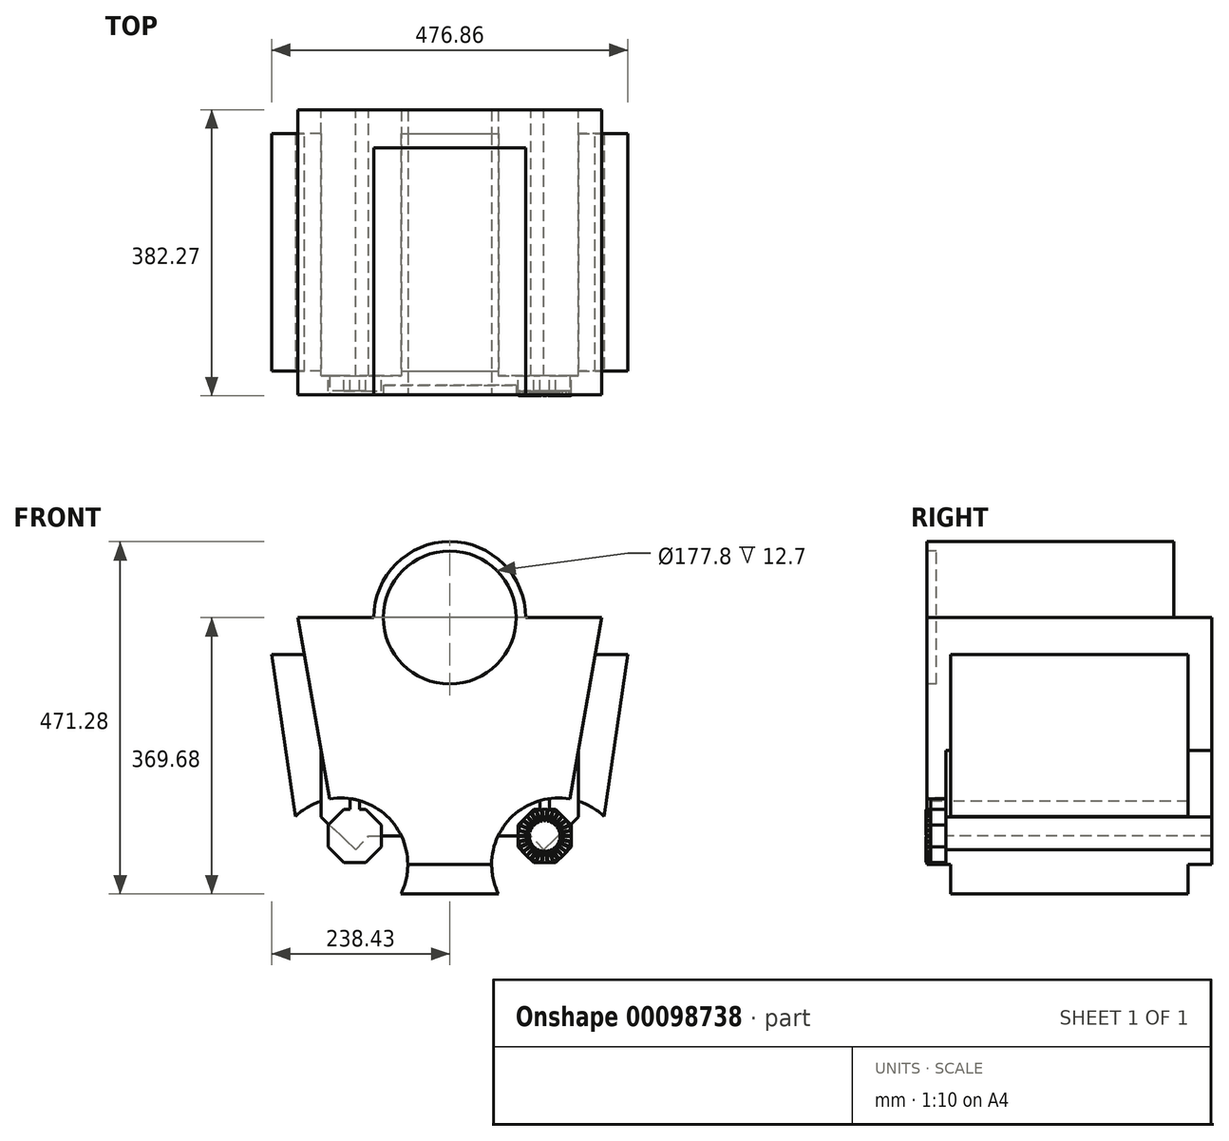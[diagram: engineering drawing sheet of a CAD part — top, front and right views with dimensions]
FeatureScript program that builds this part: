
annotation { "Feature Type Name" : "Feature", "Feature Type Description" : "" }
export const myFeature = defineFeature(function(context is Context, id is Id, definition is map)
    precondition{}
    {
        {
            var Q0;
            Q0=qCreatedBy(makeId("Front.planeOp"),FACE);
            var sketch = newSketch(context, id + "F0", { "sketchPlane" : qUnion([Q0])});
            skLineSegment(sketch, "E0", {"start": v(-144.98, -152.4) * mm, "end": v(-203.2, 177.8) * mm});
            skLineSegment(sketch, "E1", {"start": v(-203.2, 177.8) * mm, "end": v(0, 177.8) * mm});
            skLineSegment(sketch, "E2", {"start": v(-144.98, -152.4) * mm, "end": v(0, -152.4) * mm});
            skLineSegment(sketch, "E3", {"start": v(0, 177.8) * mm, "end": v(0, -152.4) * mm, "construction": true});
            skLineSegment(sketch, "E4.MirrorCS", {"start": v(203.2, 177.8) * mm, "end": v(0, 177.8) * mm});
            skLineSegment(sketch, "E5.MirrorCS", {"start": v(144.98, -152.4) * mm, "end": v(0, -152.4) * mm});
            skLineSegment(sketch, "E6.MirrorCS", {"start": v(144.98, -152.4) * mm, "end": v(203.2, 177.8) * mm});
            skSolve(sketch);
        }
        {
            var Q0;
            Q0=makeQuery(id+"F0.imprint","IMPRINT",FACE,{"disambiguationData":[TD([[makeQuery(id+"F0.imprint","IMPRINT",EDGE,{"derivedFrom":sQuery(id+"F0.wireOp",EDGE,"E0")}),-1.0]])]});
            extrude(context, id + "F1", {"entities" : qUnion([Q0]), "endBound" : BoundingType.SYMMETRIC, "depth" : 381 * mm});
        }
        {
            var Q0;
            Q0=qCreatedBy(makeId("Front.planeOp"),FACE);
            var sketch = newSketch(context, id + "F2", { "sketchPlane" : qUnion([Q0])});
            skLineSegment(sketch, "E7", {"start": v(-238.43, 128.66) * mm, "end": v(-190.8, -191.88) * mm});
            skLineSegment(sketch, "E8.MirrorCS", {"start": v(238.43, 128.66) * mm, "end": v(190.8, -191.88) * mm});
            skLineSegment(sketch, "E9", {"start": v(-238.43, 128.66) * mm, "end": v(238.43, 128.66) * mm});
            skLineSegment(sketch, "E10", {"start": v(-190.8, -191.88) * mm, "end": v(190.8, -191.88) * mm});
            skSolve(sketch);
        }
        {
            var Q0;
            Q0 = qSketchRegion(id + "F2", true);
            extrude(context, id + "F3", {"entities" : qUnion([Q0]), "operationType" : NewBodyOperationType.ADD, "endBound" : BoundingType.SYMMETRIC, "depth" : 317.5 * mm});
        }
        {
            var Q0;
            Q0=makeQuery(id+"F1.opExtrude","CAP_FACE",FACE,{"disambiguationData":[OSD([sQuery(id+"F0.wireOp",EDGE,"E0"),sQuery(id+"F0.wireOp",EDGE,"E1"),sQuery(id+"F0.wireOp",EDGE,"E2"),sQuery(id+"F0.wireOp",EDGE,"E4.MirrorCS"),sQuery(id+"F0.wireOp",EDGE,"E5.MirrorCS"),sQuery(id+"F0.wireOp",EDGE,"E6.MirrorCS")])],"isStart":false});
            var sketch = newSketch(context, id + "F4", { "sketchPlane" : qUnion([Q0])});
            skCircle(sketch, "E11", {"center": v(0, 177.8) * mm, "radius": 101.6 * mm});
            skSolve(sketch);
        }
        {
            var Q0;
            Q0 = qSketchRegion(id + "F4", true);
            extrude(context, id + "F5", {"entities" : qUnion([Q0]), "operationType" : NewBodyOperationType.ADD, "oppositeDirection" : true, "depth" : 330.2 * mm});
        }
        {
            var Q0;
            Q0=makeQuery(id+"F5.boolean.opBoolean","MERGE",FACE,{"derivedFrom":[makeQuery(id+"F1.opExtrude","CAP_FACE",FACE,{"disambiguationData":[OSD([sQuery(id+"F0.wireOp",EDGE,"E0"),sQuery(id+"F0.wireOp",EDGE,"E1"),sQuery(id+"F0.wireOp",EDGE,"E2"),sQuery(id+"F0.wireOp",EDGE,"E4.MirrorCS"),sQuery(id+"F0.wireOp",EDGE,"E5.MirrorCS"),sQuery(id+"F0.wireOp",EDGE,"E6.MirrorCS")])],"isStart":false}),makeQuery(id+"F5.opExtrude","CAP_FACE",FACE,{"disambiguationData":[OSD([sQuery(id+"F4.wireOp",EDGE,"E11")])],"isStart":true})]});
            var sketch = newSketch(context, id + "F6", { "sketchPlane" : qUnion([Q0])});
            skCircle(sketch, "E12", {"center": v(144.98, -152.4) * mm, "radius": 88.9 * mm});
            skCircle(sketch, "E13", {"center": v(-144.98, -152.4) * mm, "radius": 88.9 * mm});
            skSolve(sketch);
        }
        {
            var Q0;
            Q0 = qSketchRegion(id + "F6", true);
            extrude(context, id + "F7", {"entities" : qUnion([Q0]), "operationType" : NewBodyOperationType.REMOVE, "endBound" : BoundingType.THROUGH_ALL, "oppositeDirection" : true, "depth" : 381 * mm});
        }
        {
            var Q0;
            Q0=makeQuery(id+"F5.boolean.opBoolean","MERGE",FACE,{"derivedFrom":[makeQuery(id+"F1.opExtrude","CAP_FACE",FACE,{"disambiguationData":[OSD([sQuery(id+"F0.wireOp",EDGE,"E0"),sQuery(id+"F0.wireOp",EDGE,"E1"),sQuery(id+"F0.wireOp",EDGE,"E2"),sQuery(id+"F0.wireOp",EDGE,"E4.MirrorCS"),sQuery(id+"F0.wireOp",EDGE,"E5.MirrorCS"),sQuery(id+"F0.wireOp",EDGE,"E6.MirrorCS")])],"isStart":false}),makeQuery(id+"F5.opExtrude","CAP_FACE",FACE,{"disambiguationData":[OSD([sQuery(id+"F4.wireOp",EDGE,"E11")])],"isStart":true})]});
            var sketch = newSketch(context, id + "F8", { "sketchPlane" : qUnion([Q0])});
            skCircle(sketch, "E14", {"center": v(0, 177.8) * mm, "radius": 88.9 * mm});
            skSolve(sketch);
        }
        {
            var Q0;
            Q0 = qSketchRegion(id + "F8", true);
            extrude(context, id + "F9", {"entities" : qUnion([Q0]), "operationType" : NewBodyOperationType.REMOVE, "oppositeDirection" : true, "depth" : 12.7 * mm});
        }
        {
            var Q0;
            Q0=qCreatedBy(makeId("Front.planeOp"),FACE);
            var sketch = newSketch(context, id + "F10", { "sketchPlane" : qUnion([Q0])});
            skLineSegment(sketch, "E15.bottom", {"start": v(-171.85, 0) * mm, "end": v(171.85, 0) * mm});
            skLineSegment(sketch, "E15.left", {"start": v(-171.85, 0) * mm, "end": v(-171.85, -88.9) * mm});
            skLineSegment(sketch, "E15.right", {"start": v(171.85, 0) * mm, "end": v(171.85, -88.9) * mm});
            skLineSegment(sketch, "E16", {"start": v(-171.85, -88.9) * mm, "end": v(-125.87, -132.7) * mm});
            skLineSegment(sketch, "E17", {"start": v(-125.87, -132.7) * mm, "end": v(-108.35, -114.3) * mm});
            skLineSegment(sketch, "E18", {"start": v(0, -153.35) * mm, "end": v(0, 168.6) * mm, "construction": true});
            skPoint(sketch, "E18.endSnap0", {"position": v(0, -153.35) * mm});
            skLineSegment(sketch, "E19.MirrorCS", {"start": v(125.87, -132.7) * mm, "end": v(108.35, -114.3) * mm});
            skLineSegment(sketch, "E20.MirrorCS", {"start": v(171.85, -88.9) * mm, "end": v(125.87, -132.7) * mm});
            skLineSegment(sketch, "E21", {"start": v(-108.35, -114.3) * mm, "end": v(108.35, -114.3) * mm});
            skSolve(sketch);
        }
        {
            var Q0;
            Q0 = qSketchRegion(id + "F10", true);
            extrude(context, id + "F11", {"entities" : qUnion([Q0]), "operationType" : NewBodyOperationType.ADD, "depth" : 165.1 * mm, "hasSecondDirection" : true, "secondDirectionOppositeDirection" : true, "secondDirectionDepth" : 190.5 * mm});
        }
        {
            var Q0;
            {var subQ0=sQuery(id+"F10.wireOp",EDGE,"E19.MirrorCS");var subQ1=sQuery(id+"F10.wireOp",EDGE,"E21");var subQ2=sQuery(id+"F10.wireOp",EDGE,"E15.right");var subQ3=sQuery(id+"F10.wireOp",EDGE,"E20.MirrorCS");Q0=makeQuery(id+"F11.boolean.opBoolean","SPLIT",FACE,{"disambiguationData":[TD([makeQuery(id+"F1.opExtrude","SWEPT_FACE",FACE,{"disambiguationData":[OSD([sQuery(id+"F0.wireOp",EDGE,"E6.MirrorCS")])]})])],"derivedFrom":makeQuery(id+"F11.opExtrude","CAP_FACE",FACE,{"disambiguationData":[OSD([sQuery(id+"F10.wireOp",EDGE,"E15.bottom"),sQuery(id+"F10.wireOp",EDGE,"E15.left"),subQ2,sQuery(id+"F10.wireOp",EDGE,"E16"),sQuery(id+"F10.wireOp",EDGE,"E17"),subQ0,subQ3,subQ1])],"isStart":false})});}
            var sketch = newSketch(context, id + "F12", { "sketchPlane" : qUnion([Q0])});
            skCircle(sketch, "E22.cCircle", {"center": v(127, -114.3) * mm, "radius": 35.56 * mm, "construction": true});
            skLineSegment(sketch, "E22.0", {"start": v(112.27, -78.74) * mm, "end": v(120.65, -78.74) * mm});
            skLineSegment(sketch, "E22.1", {"start": v(141.73, -78.74) * mm, "end": v(162.56, -99.57) * mm});
            skLineSegment(sketch, "E22.2", {"start": v(162.56, -99.57) * mm, "end": v(162.56, -129.03) * mm});
            skLineSegment(sketch, "E22.3", {"start": v(162.56, -129.03) * mm, "end": v(141.73, -149.86) * mm});
            skLineSegment(sketch, "E22.4", {"start": v(141.73, -149.86) * mm, "end": v(112.27, -149.86) * mm});
            skLineSegment(sketch, "E22.5", {"start": v(112.27, -149.86) * mm, "end": v(91.44, -129.03) * mm});
            skLineSegment(sketch, "E22.6", {"start": v(91.44, -129.03) * mm, "end": v(91.44, -99.57) * mm});
            skLineSegment(sketch, "E22.7", {"start": v(91.44, -99.57) * mm, "end": v(112.27, -78.74) * mm});
            skPoint(sketch, "E22.0.midPoint", {"position": v(127, -78.74) * mm});
            skLineSegment(sketch, "E23", {"start": v(120.65, -78.74) * mm, "end": v(120.65, -66.9) * mm});
            skLineSegment(sketch, "E24", {"start": v(133.35, -78.74) * mm, "end": v(133.35, -64.26) * mm});
            skArc(sketch, "E25", {"start": v(133.35, -64.26) * mm, "mid": v(126.95, -65.35) * mm, "end": v(120.65, -66.9) * mm});
            skLineSegment(sketch, "E26.trimOffspring", {"start": v(133.35, -78.74) * mm, "end": v(141.73, -78.74) * mm});
            skLineSegment(sketch, "E27.MirrorCS", {"start": v(-133.35, -78.74) * mm, "end": v(-141.73, -78.74) * mm});
            skLineSegment(sketch, "E28.MirrorCS", {"start": v(-112.27, -78.74) * mm, "end": v(-120.65, -78.74) * mm});
            skLineSegment(sketch, "E29.MirrorCS", {"start": v(-120.65, -78.74) * mm, "end": v(-120.65, -66.9) * mm});
            skLineSegment(sketch, "E30.MirrorCS", {"start": v(-91.44, -129.03) * mm, "end": v(-91.44, -99.57) * mm});
            skLineSegment(sketch, "E31.MirrorCS", {"start": v(-141.73, -78.74) * mm, "end": v(-162.56, -99.57) * mm});
            skLineSegment(sketch, "E32.MirrorCS", {"start": v(-112.27, -149.86) * mm, "end": v(-91.44, -129.03) * mm});
            skLineSegment(sketch, "E33.MirrorCS", {"start": v(-141.73, -149.86) * mm, "end": v(-112.27, -149.86) * mm});
            skLineSegment(sketch, "E34.MirrorCS", {"start": v(-133.35, -78.74) * mm, "end": v(-133.35, -64.26) * mm});
            skLineSegment(sketch, "E35.MirrorCS", {"start": v(-91.44, -99.57) * mm, "end": v(-112.27, -78.74) * mm});
            skPoint(sketch, "E36.MirrorP", {"position": v(-127, -78.74) * mm});
            skCircle(sketch, "E37.MirrorC", {"center": v(-127, -114.3) * mm, "radius": 35.56 * mm, "construction": true});
            skArc(sketch, "E38.MirrorCS", {"start": v(-133.35, -64.26) * mm, "mid": v(-126.95, -65.35) * mm, "end": v(-120.65, -66.9) * mm});
            skLineSegment(sketch, "E39.MirrorCS", {"start": v(-162.56, -99.57) * mm, "end": v(-162.56, -129.03) * mm});
            skLineSegment(sketch, "E40.MirrorCS", {"start": v(-162.56, -129.03) * mm, "end": v(-141.73, -149.86) * mm});
            skSolve(sketch);
        }
        {
            var Q0;
            Q0 = qSketchRegion(id + "F12", true);
            extrude(context, id + "F13", {"entities" : qUnion([Q0]), "operationType" : NewBodyOperationType.ADD, "depth" : 20.32 * mm});
        }
        {
            var Q0;
            Q0=makeQuery(id+"F13.opExtrude","CAP_FACE",FACE,{"disambiguationData":[OSD([sQuery(id+"F12.wireOp",EDGE,"E22.0"),sQuery(id+"F12.wireOp",EDGE,"E22.1"),sQuery(id+"F12.wireOp",EDGE,"E22.2"),sQuery(id+"F12.wireOp",EDGE,"E22.3"),sQuery(id+"F12.wireOp",EDGE,"E22.4"),sQuery(id+"F12.wireOp",EDGE,"E22.5"),sQuery(id+"F12.wireOp",EDGE,"E22.6"),sQuery(id+"F12.wireOp",EDGE,"E22.7"),sQuery(id+"F12.wireOp",EDGE,"E23"),sQuery(id+"F12.wireOp",EDGE,"E24"),sQuery(id+"F12.wireOp",EDGE,"E25"),sQuery(id+"F12.wireOp",EDGE,"E26.trimOffspring")])],"isStart":false});
            var sketch = newSketch(context, id + "F14", { "sketchPlane" : qUnion([Q0])});
            skLineSegment(sketch, "E41", {"start": v(127, -149.86) * mm, "end": v(127, 211.19) * mm, "construction": true});
            skLineSegment(sketch, "E42", {"start": v(91.44, -114.3) * mm, "end": v(162.56, -114.3) * mm, "construction": true});
            skCircle(sketch, "E43", {"center": v(127, -114.3) * mm, "radius": 35.56 * mm, "construction": true});
            skCircle(sketch, "E44", {"center": v(127, -114.3) * mm, "radius": 20.32 * mm, "construction": true});
            skLineSegment(sketch, "E45", {"start": v(130.26, -78.89) * mm, "end": v(128.27, -94.02) * mm});
            skLineSegment(sketch, "E46.MirrorCS", {"start": v(123.74, -78.89) * mm, "end": v(125.73, -94.02) * mm});
            skArc(sketch, "E47", {"start": v(123.74, -78.89) * mm, "mid": v(127, -78.74) * mm, "end": v(130.26, -78.89) * mm});
            skArc(sketch, "E48", {"start": v(125.73, -94.02) * mm, "mid": v(127, -93.98) * mm, "end": v(128.27, -94.02) * mm});
            skLineSegment(sketch, "E49.1.0", {"start": v(116.45, -80.34) * mm, "end": v(121.54, -94.73) * mm});
            skLineSegment(sketch, "E49.1.1", {"start": v(122.83, -78.99) * mm, "end": v(124.03, -94.2) * mm});
            skArc(sketch, "E49.1.2", {"start": v(116.45, -80.34) * mm, "mid": v(119.6, -79.52) * mm, "end": v(122.83, -78.99) * mm});
            skArc(sketch, "E49.1.3", {"start": v(121.54, -94.73) * mm, "mid": v(122.78, -94.42) * mm, "end": v(124.03, -94.2) * mm});
            skLineSegment(sketch, "E49.2.0", {"start": v(109.62, -83.28) * mm, "end": v(117.6, -96.29) * mm});
            skLineSegment(sketch, "E49.2.1", {"start": v(115.58, -80.62) * mm, "end": v(119.91, -95.26) * mm});
            skArc(sketch, "E49.2.2", {"start": v(109.62, -83.28) * mm, "mid": v(112.54, -81.81) * mm, "end": v(115.58, -80.62) * mm});
            skArc(sketch, "E49.2.3", {"start": v(117.6, -96.29) * mm, "mid": v(118.74, -95.74) * mm, "end": v(119.91, -95.26) * mm});
            skLineSegment(sketch, "E49.3.0", {"start": v(103.55, -87.57) * mm, "end": v(114.05, -98.64) * mm});
            skLineSegment(sketch, "E49.3.1", {"start": v(108.83, -83.74) * mm, "end": v(116.1, -97.15) * mm});
            skArc(sketch, "E49.3.2", {"start": v(103.55, -87.57) * mm, "mid": v(106.1, -85.53) * mm, "end": v(108.83, -83.74) * mm});
            skArc(sketch, "E49.3.3", {"start": v(114.05, -98.64) * mm, "mid": v(115.06, -97.86) * mm, "end": v(116.1, -97.15) * mm});
            skLineSegment(sketch, "E49.4.0", {"start": v(98.5, -93.03) * mm, "end": v(111.08, -101.67) * mm});
            skLineSegment(sketch, "E49.4.1", {"start": v(102.87, -88.18) * mm, "end": v(112.78, -99.79) * mm});
            skArc(sketch, "E49.4.2", {"start": v(98.5, -93.03) * mm, "mid": v(100.57, -90.5) * mm, "end": v(102.87, -88.18) * mm});
            skArc(sketch, "E49.4.3", {"start": v(111.08, -101.67) * mm, "mid": v(111.9, -100.7) * mm, "end": v(112.78, -99.79) * mm});
            skLineSegment(sketch, "E49.5.0", {"start": v(94.7, -99.42) * mm, "end": v(108.8, -105.26) * mm});
            skLineSegment(sketch, "E49.5.1", {"start": v(97.96, -93.77) * mm, "end": v(110.07, -103.06) * mm});
            skArc(sketch, "E49.5.2", {"start": v(94.7, -99.42) * mm, "mid": v(96.2, -96.52) * mm, "end": v(97.96, -93.77) * mm});
            skArc(sketch, "E49.5.3", {"start": v(108.8, -105.26) * mm, "mid": v(109.4, -104.14) * mm, "end": v(110.07, -103.06) * mm});
            skLineSegment(sketch, "E49.6.0", {"start": v(92.32, -106.46) * mm, "end": v(107.32, -109.24) * mm});
            skLineSegment(sketch, "E49.6.1", {"start": v(94.33, -100.26) * mm, "end": v(108.1, -106.83) * mm});
            skArc(sketch, "E49.6.2", {"start": v(92.32, -106.46) * mm, "mid": v(93.18, -103.31) * mm, "end": v(94.33, -100.26) * mm});
            skArc(sketch, "E49.6.3", {"start": v(107.32, -109.24) * mm, "mid": v(107.67, -108.02) * mm, "end": v(108.1, -106.83) * mm});
            skLineSegment(sketch, "E49.7.0", {"start": v(91.44, -113.84) * mm, "end": v(106.7, -113.44) * mm});
            skLineSegment(sketch, "E49.7.1", {"start": v(92.12, -107.35) * mm, "end": v(106.96, -110.92) * mm});
            skArc(sketch, "E49.7.2", {"start": v(91.44, -113.84) * mm, "mid": v(91.63, -110.58) * mm, "end": v(92.12, -107.35) * mm});
            skArc(sketch, "E49.7.3", {"start": v(106.7, -113.44) * mm, "mid": v(106.8, -112.18) * mm, "end": v(106.96, -110.92) * mm});
            skLineSegment(sketch, "E49.8.0", {"start": v(92.12, -121.25) * mm, "end": v(106.96, -117.68) * mm});
            skLineSegment(sketch, "E49.8.1", {"start": v(91.44, -114.76) * mm, "end": v(106.7, -115.16) * mm});
            skArc(sketch, "E49.8.2", {"start": v(92.12, -121.25) * mm, "mid": v(91.63, -118.02) * mm, "end": v(91.44, -114.76) * mm});
            skArc(sketch, "E49.8.3", {"start": v(106.96, -117.68) * mm, "mid": v(106.8, -116.42) * mm, "end": v(106.7, -115.16) * mm});
            skLineSegment(sketch, "E49.9.0", {"start": v(94.33, -128.34) * mm, "end": v(108.1, -121.77) * mm});
            skLineSegment(sketch, "E49.9.1", {"start": v(92.32, -122.14) * mm, "end": v(107.32, -119.36) * mm});
            skArc(sketch, "E49.9.2", {"start": v(94.33, -128.34) * mm, "mid": v(93.18, -125.29) * mm, "end": v(92.32, -122.14) * mm});
            skArc(sketch, "E49.9.3", {"start": v(108.1, -121.77) * mm, "mid": v(107.67, -120.58) * mm, "end": v(107.32, -119.36) * mm});
            skLineSegment(sketch, "E49.10.0", {"start": v(97.96, -134.83) * mm, "end": v(110.07, -125.54) * mm});
            skLineSegment(sketch, "E49.10.1", {"start": v(94.7, -129.18) * mm, "end": v(108.8, -123.34) * mm});
            skArc(sketch, "E49.10.2", {"start": v(97.96, -134.83) * mm, "mid": v(96.2, -132.08) * mm, "end": v(94.7, -129.18) * mm});
            skArc(sketch, "E49.10.3", {"start": v(110.07, -125.54) * mm, "mid": v(109.4, -124.46) * mm, "end": v(108.8, -123.34) * mm});
            skLineSegment(sketch, "E49.11.0", {"start": v(102.87, -140.42) * mm, "end": v(112.78, -128.81) * mm});
            skLineSegment(sketch, "E49.11.1", {"start": v(98.5, -135.57) * mm, "end": v(111.08, -126.93) * mm});
            skArc(sketch, "E49.11.2", {"start": v(102.87, -140.42) * mm, "mid": v(100.57, -138.1) * mm, "end": v(98.5, -135.57) * mm});
            skArc(sketch, "E49.11.3", {"start": v(112.78, -128.81) * mm, "mid": v(111.9, -127.9) * mm, "end": v(111.08, -126.93) * mm});
            skLineSegment(sketch, "E49.12.0", {"start": v(108.83, -144.86) * mm, "end": v(116.1, -131.45) * mm});
            skLineSegment(sketch, "E49.12.1", {"start": v(103.55, -141.03) * mm, "end": v(114.05, -129.96) * mm});
            skArc(sketch, "E49.12.2", {"start": v(108.83, -144.86) * mm, "mid": v(106.1, -143.07) * mm, "end": v(103.55, -141.03) * mm});
            skArc(sketch, "E49.12.3", {"start": v(116.1, -131.45) * mm, "mid": v(115.06, -130.74) * mm, "end": v(114.05, -129.96) * mm});
            skLineSegment(sketch, "E49.13.0", {"start": v(115.58, -147.98) * mm, "end": v(119.91, -133.34) * mm});
            skLineSegment(sketch, "E49.13.1", {"start": v(109.62, -145.32) * mm, "end": v(117.6, -132.31) * mm});
            skArc(sketch, "E49.13.2", {"start": v(115.58, -147.98) * mm, "mid": v(112.54, -146.79) * mm, "end": v(109.62, -145.32) * mm});
            skArc(sketch, "E49.13.3", {"start": v(119.91, -133.34) * mm, "mid": v(118.74, -132.86) * mm, "end": v(117.6, -132.31) * mm});
            skLineSegment(sketch, "E49.14.0", {"start": v(122.83, -149.61) * mm, "end": v(124.03, -134.4) * mm});
            skLineSegment(sketch, "E49.14.1", {"start": v(116.45, -148.26) * mm, "end": v(121.54, -133.87) * mm});
            skArc(sketch, "E49.14.2", {"start": v(122.83, -149.61) * mm, "mid": v(119.6, -149.08) * mm, "end": v(116.45, -148.26) * mm});
            skArc(sketch, "E49.14.3", {"start": v(124.03, -134.4) * mm, "mid": v(122.78, -134.18) * mm, "end": v(121.54, -133.87) * mm});
            skLineSegment(sketch, "E49.15.0", {"start": v(130.26, -149.71) * mm, "end": v(128.27, -134.58) * mm});
            skLineSegment(sketch, "E49.15.1", {"start": v(123.74, -149.71) * mm, "end": v(125.73, -134.58) * mm});
            skArc(sketch, "E49.15.2", {"start": v(130.26, -149.71) * mm, "mid": v(127, -149.86) * mm, "end": v(123.74, -149.71) * mm});
            skArc(sketch, "E49.15.3", {"start": v(128.27, -134.58) * mm, "mid": v(127, -134.62) * mm, "end": v(125.73, -134.58) * mm});
            skLineSegment(sketch, "E49.16.0", {"start": v(137.55, -148.26) * mm, "end": v(132.46, -133.87) * mm});
            skLineSegment(sketch, "E49.16.1", {"start": v(131.17, -149.61) * mm, "end": v(129.97, -134.4) * mm});
            skArc(sketch, "E49.16.2", {"start": v(137.55, -148.26) * mm, "mid": v(134.4, -149.08) * mm, "end": v(131.17, -149.61) * mm});
            skArc(sketch, "E49.16.3", {"start": v(132.46, -133.87) * mm, "mid": v(131.22, -134.18) * mm, "end": v(129.97, -134.4) * mm});
            skLineSegment(sketch, "E49.17.0", {"start": v(144.38, -145.32) * mm, "end": v(136.4, -132.31) * mm});
            skLineSegment(sketch, "E49.17.1", {"start": v(138.42, -147.98) * mm, "end": v(134.09, -133.34) * mm});
            skArc(sketch, "E49.17.2", {"start": v(144.38, -145.32) * mm, "mid": v(141.46, -146.79) * mm, "end": v(138.42, -147.98) * mm});
            skArc(sketch, "E49.17.3", {"start": v(136.4, -132.31) * mm, "mid": v(135.26, -132.86) * mm, "end": v(134.09, -133.34) * mm});
            skLineSegment(sketch, "E49.18.0", {"start": v(150.45, -141.03) * mm, "end": v(139.95, -129.96) * mm});
            skLineSegment(sketch, "E49.18.1", {"start": v(145.17, -144.86) * mm, "end": v(137.9, -131.45) * mm});
            skArc(sketch, "E49.18.2", {"start": v(150.45, -141.03) * mm, "mid": v(147.9, -143.07) * mm, "end": v(145.17, -144.86) * mm});
            skArc(sketch, "E49.18.3", {"start": v(139.95, -129.96) * mm, "mid": v(138.94, -130.74) * mm, "end": v(137.9, -131.45) * mm});
            skLineSegment(sketch, "E49.19.0", {"start": v(155.5, -135.57) * mm, "end": v(142.92, -126.93) * mm});
            skLineSegment(sketch, "E49.19.1", {"start": v(151.13, -140.42) * mm, "end": v(141.22, -128.81) * mm});
            skArc(sketch, "E49.19.2", {"start": v(155.5, -135.57) * mm, "mid": v(153.43, -138.1) * mm, "end": v(151.13, -140.42) * mm});
            skArc(sketch, "E49.19.3", {"start": v(142.92, -126.93) * mm, "mid": v(142.1, -127.9) * mm, "end": v(141.22, -128.81) * mm});
            skLineSegment(sketch, "E49.20.0", {"start": v(159.3, -129.18) * mm, "end": v(145.2, -123.34) * mm});
            skLineSegment(sketch, "E49.20.1", {"start": v(156.04, -134.83) * mm, "end": v(143.93, -125.54) * mm});
            skArc(sketch, "E49.20.2", {"start": v(159.3, -129.18) * mm, "mid": v(157.8, -132.08) * mm, "end": v(156.04, -134.83) * mm});
            skArc(sketch, "E49.20.3", {"start": v(145.2, -123.34) * mm, "mid": v(144.6, -124.46) * mm, "end": v(143.93, -125.54) * mm});
            skLineSegment(sketch, "E49.21.0", {"start": v(161.68, -122.14) * mm, "end": v(146.68, -119.36) * mm});
            skLineSegment(sketch, "E49.21.1", {"start": v(159.67, -128.34) * mm, "end": v(145.9, -121.77) * mm});
            skArc(sketch, "E49.21.2", {"start": v(161.68, -122.14) * mm, "mid": v(160.82, -125.29) * mm, "end": v(159.67, -128.34) * mm});
            skArc(sketch, "E49.21.3", {"start": v(146.68, -119.36) * mm, "mid": v(146.33, -120.58) * mm, "end": v(145.9, -121.77) * mm});
            skLineSegment(sketch, "E49.22.0", {"start": v(162.56, -114.76) * mm, "end": v(147.3, -115.16) * mm});
            skLineSegment(sketch, "E49.22.1", {"start": v(161.88, -121.25) * mm, "end": v(147.04, -117.68) * mm});
            skArc(sketch, "E49.22.2", {"start": v(162.56, -114.76) * mm, "mid": v(162.37, -118.02) * mm, "end": v(161.88, -121.25) * mm});
            skArc(sketch, "E49.22.3", {"start": v(147.3, -115.16) * mm, "mid": v(147.2, -116.42) * mm, "end": v(147.04, -117.68) * mm});
            skLineSegment(sketch, "E49.23.0", {"start": v(161.88, -107.35) * mm, "end": v(147.04, -110.92) * mm});
            skLineSegment(sketch, "E49.23.1", {"start": v(162.56, -113.84) * mm, "end": v(147.3, -113.44) * mm});
            skArc(sketch, "E49.23.2", {"start": v(161.88, -107.35) * mm, "mid": v(162.37, -110.58) * mm, "end": v(162.56, -113.84) * mm});
            skArc(sketch, "E49.23.3", {"start": v(147.04, -110.92) * mm, "mid": v(147.2, -112.18) * mm, "end": v(147.3, -113.44) * mm});
            skLineSegment(sketch, "E49.24.0", {"start": v(159.67, -100.26) * mm, "end": v(145.9, -106.83) * mm});
            skLineSegment(sketch, "E49.24.1", {"start": v(161.68, -106.46) * mm, "end": v(146.68, -109.24) * mm});
            skArc(sketch, "E49.24.2", {"start": v(159.67, -100.26) * mm, "mid": v(160.82, -103.31) * mm, "end": v(161.68, -106.46) * mm});
            skArc(sketch, "E49.24.3", {"start": v(145.9, -106.83) * mm, "mid": v(146.33, -108.02) * mm, "end": v(146.68, -109.24) * mm});
            skLineSegment(sketch, "E49.25.0", {"start": v(156.04, -93.77) * mm, "end": v(143.93, -103.06) * mm});
            skLineSegment(sketch, "E49.25.1", {"start": v(159.3, -99.42) * mm, "end": v(145.2, -105.26) * mm});
            skArc(sketch, "E49.25.2", {"start": v(156.04, -93.77) * mm, "mid": v(157.8, -96.52) * mm, "end": v(159.3, -99.42) * mm});
            skArc(sketch, "E49.25.3", {"start": v(143.93, -103.06) * mm, "mid": v(144.6, -104.14) * mm, "end": v(145.2, -105.26) * mm});
            skLineSegment(sketch, "E49.26.0", {"start": v(151.13, -88.18) * mm, "end": v(141.22, -99.79) * mm});
            skLineSegment(sketch, "E49.26.1", {"start": v(155.5, -93.03) * mm, "end": v(142.92, -101.67) * mm});
            skArc(sketch, "E49.26.2", {"start": v(151.13, -88.18) * mm, "mid": v(153.43, -90.5) * mm, "end": v(155.5, -93.03) * mm});
            skArc(sketch, "E49.26.3", {"start": v(141.22, -99.79) * mm, "mid": v(142.1, -100.7) * mm, "end": v(142.92, -101.67) * mm});
            skLineSegment(sketch, "E49.27.0", {"start": v(145.17, -83.74) * mm, "end": v(137.9, -97.15) * mm});
            skLineSegment(sketch, "E49.27.1", {"start": v(150.45, -87.57) * mm, "end": v(139.95, -98.64) * mm});
            skArc(sketch, "E49.27.2", {"start": v(145.17, -83.74) * mm, "mid": v(147.9, -85.53) * mm, "end": v(150.45, -87.57) * mm});
            skArc(sketch, "E49.27.3", {"start": v(137.9, -97.15) * mm, "mid": v(138.94, -97.86) * mm, "end": v(139.95, -98.64) * mm});
            skLineSegment(sketch, "E49.28.0", {"start": v(138.42, -80.62) * mm, "end": v(134.09, -95.26) * mm});
            skLineSegment(sketch, "E49.28.1", {"start": v(144.38, -83.28) * mm, "end": v(136.4, -96.29) * mm});
            skArc(sketch, "E49.28.2", {"start": v(138.42, -80.62) * mm, "mid": v(141.46, -81.81) * mm, "end": v(144.38, -83.28) * mm});
            skArc(sketch, "E49.28.3", {"start": v(134.09, -95.26) * mm, "mid": v(135.26, -95.74) * mm, "end": v(136.4, -96.29) * mm});
            skLineSegment(sketch, "E49.29.0", {"start": v(131.17, -78.99) * mm, "end": v(129.97, -94.2) * mm});
            skLineSegment(sketch, "E49.29.1", {"start": v(137.55, -80.34) * mm, "end": v(132.46, -94.73) * mm});
            skArc(sketch, "E49.29.2", {"start": v(131.17, -78.99) * mm, "mid": v(134.4, -79.52) * mm, "end": v(137.55, -80.34) * mm});
            skArc(sketch, "E49.29.3", {"start": v(129.97, -94.2) * mm, "mid": v(131.22, -94.42) * mm, "end": v(132.46, -94.73) * mm});
            skSolve(sketch);
        }
        {
            var Q0;
            Q0 = qSketchRegion(id + "F14", true);
            extrude(context, id + "F15", {"entities" : qUnion([Q0]), "operationType" : NewBodyOperationType.ADD, "depth" : 6.35 * mm});
        }
        {
            var Q0;
            Q0=makeQuery(id+"F15.opExtrude","CAP_FACE",FACE,{"disambiguationData":[OSD([sQuery(id+"F14.wireOp",EDGE,"E49.29.0"),sQuery(id+"F14.wireOp",EDGE,"E49.29.1"),sQuery(id+"F14.wireOp",EDGE,"E49.29.2"),sQuery(id+"F14.wireOp",EDGE,"E49.29.3")])],"isStart":false});
            var Q1;
            Q1=makeQuery(id+"F15.opExtrude","CAP_FACE",FACE,{"disambiguationData":[OSD([sQuery(id+"F14.wireOp",EDGE,"E45"),sQuery(id+"F14.wireOp",EDGE,"E46.MirrorCS"),sQuery(id+"F14.wireOp",EDGE,"E47"),sQuery(id+"F14.wireOp",EDGE,"E48")])],"isStart":false});
            var Q2;
            Q2=makeQuery(id+"F15.opExtrude","CAP_FACE",FACE,{"disambiguationData":[OSD([sQuery(id+"F14.wireOp",EDGE,"E49.28.0"),sQuery(id+"F14.wireOp",EDGE,"E49.28.1"),sQuery(id+"F14.wireOp",EDGE,"E49.28.2"),sQuery(id+"F14.wireOp",EDGE,"E49.28.3")])],"isStart":false});
            var Q3;
            Q3=makeQuery(id+"F15.opExtrude","CAP_FACE",FACE,{"disambiguationData":[OSD([sQuery(id+"F14.wireOp",EDGE,"E49.27.0"),sQuery(id+"F14.wireOp",EDGE,"E49.27.1"),sQuery(id+"F14.wireOp",EDGE,"E49.27.2"),sQuery(id+"F14.wireOp",EDGE,"E49.27.3")])],"isStart":false});
            var Q4;
            Q4=makeQuery(id+"F15.opExtrude","CAP_FACE",FACE,{"disambiguationData":[OSD([sQuery(id+"F14.wireOp",EDGE,"E49.26.0"),sQuery(id+"F14.wireOp",EDGE,"E49.26.1"),sQuery(id+"F14.wireOp",EDGE,"E49.26.2"),sQuery(id+"F14.wireOp",EDGE,"E49.26.3")])],"isStart":false});
            var Q5;
            Q5=makeQuery(id+"F15.opExtrude","CAP_FACE",FACE,{"disambiguationData":[OSD([sQuery(id+"F14.wireOp",EDGE,"E49.25.0"),sQuery(id+"F14.wireOp",EDGE,"E49.25.1"),sQuery(id+"F14.wireOp",EDGE,"E49.25.2"),sQuery(id+"F14.wireOp",EDGE,"E49.25.3")])],"isStart":false});
            var Q6;
            Q6=makeQuery(id+"F15.opExtrude","CAP_FACE",FACE,{"disambiguationData":[OSD([sQuery(id+"F14.wireOp",EDGE,"E49.24.0"),sQuery(id+"F14.wireOp",EDGE,"E49.24.1"),sQuery(id+"F14.wireOp",EDGE,"E49.24.2"),sQuery(id+"F14.wireOp",EDGE,"E49.24.3")])],"isStart":false});
            var Q7;
            Q7=makeQuery(id+"F15.opExtrude","CAP_FACE",FACE,{"disambiguationData":[OSD([sQuery(id+"F14.wireOp",EDGE,"E49.23.0"),sQuery(id+"F14.wireOp",EDGE,"E49.23.1"),sQuery(id+"F14.wireOp",EDGE,"E49.23.2"),sQuery(id+"F14.wireOp",EDGE,"E49.23.3")])],"isStart":false});
            var Q8;
            Q8=makeQuery(id+"F15.opExtrude","CAP_FACE",FACE,{"disambiguationData":[OSD([sQuery(id+"F14.wireOp",EDGE,"E49.22.0"),sQuery(id+"F14.wireOp",EDGE,"E49.22.1"),sQuery(id+"F14.wireOp",EDGE,"E49.22.2"),sQuery(id+"F14.wireOp",EDGE,"E49.22.3")])],"isStart":false});
            var Q9;
            Q9=makeQuery(id+"F15.opExtrude","CAP_FACE",FACE,{"disambiguationData":[OSD([sQuery(id+"F14.wireOp",EDGE,"E49.21.0"),sQuery(id+"F14.wireOp",EDGE,"E49.21.1"),sQuery(id+"F14.wireOp",EDGE,"E49.21.2"),sQuery(id+"F14.wireOp",EDGE,"E49.21.3")])],"isStart":false});
            var Q10;
            Q10=makeQuery(id+"F15.opExtrude","CAP_FACE",FACE,{"disambiguationData":[OSD([sQuery(id+"F14.wireOp",EDGE,"E49.20.0"),sQuery(id+"F14.wireOp",EDGE,"E49.20.1"),sQuery(id+"F14.wireOp",EDGE,"E49.20.2"),sQuery(id+"F14.wireOp",EDGE,"E49.20.3")])],"isStart":false});
            var Q11;
            Q11=makeQuery(id+"F15.opExtrude","CAP_FACE",FACE,{"disambiguationData":[OSD([sQuery(id+"F14.wireOp",EDGE,"E49.19.0"),sQuery(id+"F14.wireOp",EDGE,"E49.19.1"),sQuery(id+"F14.wireOp",EDGE,"E49.19.2"),sQuery(id+"F14.wireOp",EDGE,"E49.19.3")])],"isStart":false});
            var Q12;
            Q12=makeQuery(id+"F15.opExtrude","CAP_FACE",FACE,{"disambiguationData":[OSD([sQuery(id+"F14.wireOp",EDGE,"E49.18.0"),sQuery(id+"F14.wireOp",EDGE,"E49.18.1"),sQuery(id+"F14.wireOp",EDGE,"E49.18.2"),sQuery(id+"F14.wireOp",EDGE,"E49.18.3")])],"isStart":false});
            var Q13;
            Q13=makeQuery(id+"F15.opExtrude","CAP_FACE",FACE,{"disambiguationData":[OSD([sQuery(id+"F14.wireOp",EDGE,"E49.17.0"),sQuery(id+"F14.wireOp",EDGE,"E49.17.1"),sQuery(id+"F14.wireOp",EDGE,"E49.17.2"),sQuery(id+"F14.wireOp",EDGE,"E49.17.3")])],"isStart":false});
            var Q14;
            Q14=makeQuery(id+"F15.opExtrude","CAP_FACE",FACE,{"disambiguationData":[OSD([sQuery(id+"F14.wireOp",EDGE,"E49.16.0"),sQuery(id+"F14.wireOp",EDGE,"E49.16.1"),sQuery(id+"F14.wireOp",EDGE,"E49.16.2"),sQuery(id+"F14.wireOp",EDGE,"E49.16.3")])],"isStart":false});
            var Q15;
            Q15=makeQuery(id+"F15.opExtrude","CAP_FACE",FACE,{"disambiguationData":[OSD([sQuery(id+"F14.wireOp",EDGE,"E49.15.0"),sQuery(id+"F14.wireOp",EDGE,"E49.15.1"),sQuery(id+"F14.wireOp",EDGE,"E49.15.2"),sQuery(id+"F14.wireOp",EDGE,"E49.15.3")])],"isStart":false});
            var Q16;
            Q16=makeQuery(id+"F15.opExtrude","CAP_FACE",FACE,{"disambiguationData":[OSD([sQuery(id+"F14.wireOp",EDGE,"E49.14.0"),sQuery(id+"F14.wireOp",EDGE,"E49.14.1"),sQuery(id+"F14.wireOp",EDGE,"E49.14.2"),sQuery(id+"F14.wireOp",EDGE,"E49.14.3")])],"isStart":false});
            var Q17;
            Q17=makeQuery(id+"F15.opExtrude","CAP_FACE",FACE,{"disambiguationData":[OSD([sQuery(id+"F14.wireOp",EDGE,"E49.13.0"),sQuery(id+"F14.wireOp",EDGE,"E49.13.1"),sQuery(id+"F14.wireOp",EDGE,"E49.13.2"),sQuery(id+"F14.wireOp",EDGE,"E49.13.3")])],"isStart":false});
            var Q18;
            Q18=makeQuery(id+"F15.opExtrude","CAP_FACE",FACE,{"disambiguationData":[OSD([sQuery(id+"F14.wireOp",EDGE,"E49.12.0"),sQuery(id+"F14.wireOp",EDGE,"E49.12.1"),sQuery(id+"F14.wireOp",EDGE,"E49.12.2"),sQuery(id+"F14.wireOp",EDGE,"E49.12.3")])],"isStart":false});
            var Q19;
            Q19=makeQuery(id+"F15.opExtrude","CAP_FACE",FACE,{"disambiguationData":[OSD([sQuery(id+"F14.wireOp",EDGE,"E49.11.0"),sQuery(id+"F14.wireOp",EDGE,"E49.11.1"),sQuery(id+"F14.wireOp",EDGE,"E49.11.2"),sQuery(id+"F14.wireOp",EDGE,"E49.11.3")])],"isStart":false});
            var Q20;
            Q20=makeQuery(id+"F15.opExtrude","CAP_FACE",FACE,{"disambiguationData":[OSD([sQuery(id+"F14.wireOp",EDGE,"E49.10.0"),sQuery(id+"F14.wireOp",EDGE,"E49.10.1"),sQuery(id+"F14.wireOp",EDGE,"E49.10.2"),sQuery(id+"F14.wireOp",EDGE,"E49.10.3")])],"isStart":false});
            var Q21;
            Q21=makeQuery(id+"F15.opExtrude","CAP_FACE",FACE,{"disambiguationData":[OSD([sQuery(id+"F14.wireOp",EDGE,"E49.9.0"),sQuery(id+"F14.wireOp",EDGE,"E49.9.1"),sQuery(id+"F14.wireOp",EDGE,"E49.9.2"),sQuery(id+"F14.wireOp",EDGE,"E49.9.3")])],"isStart":false});
            var Q22;
            Q22=makeQuery(id+"F15.opExtrude","CAP_FACE",FACE,{"disambiguationData":[OSD([sQuery(id+"F14.wireOp",EDGE,"E49.8.0"),sQuery(id+"F14.wireOp",EDGE,"E49.8.1"),sQuery(id+"F14.wireOp",EDGE,"E49.8.2"),sQuery(id+"F14.wireOp",EDGE,"E49.8.3")])],"isStart":false});
            var Q23;
            Q23=makeQuery(id+"F15.opExtrude","CAP_FACE",FACE,{"disambiguationData":[OSD([sQuery(id+"F14.wireOp",EDGE,"E49.7.0"),sQuery(id+"F14.wireOp",EDGE,"E49.7.1"),sQuery(id+"F14.wireOp",EDGE,"E49.7.2"),sQuery(id+"F14.wireOp",EDGE,"E49.7.3")])],"isStart":false});
            var Q24;
            Q24=makeQuery(id+"F15.opExtrude","CAP_FACE",FACE,{"disambiguationData":[OSD([sQuery(id+"F14.wireOp",EDGE,"E49.6.0"),sQuery(id+"F14.wireOp",EDGE,"E49.6.1"),sQuery(id+"F14.wireOp",EDGE,"E49.6.2"),sQuery(id+"F14.wireOp",EDGE,"E49.6.3")])],"isStart":false});
            var Q25;
            Q25=makeQuery(id+"F15.opExtrude","CAP_FACE",FACE,{"disambiguationData":[OSD([sQuery(id+"F14.wireOp",EDGE,"E49.5.0"),sQuery(id+"F14.wireOp",EDGE,"E49.5.1"),sQuery(id+"F14.wireOp",EDGE,"E49.5.2"),sQuery(id+"F14.wireOp",EDGE,"E49.5.3")])],"isStart":false});
            var Q26;
            Q26=makeQuery(id+"F15.opExtrude","CAP_FACE",FACE,{"disambiguationData":[OSD([sQuery(id+"F14.wireOp",EDGE,"E49.4.0"),sQuery(id+"F14.wireOp",EDGE,"E49.4.1"),sQuery(id+"F14.wireOp",EDGE,"E49.4.2"),sQuery(id+"F14.wireOp",EDGE,"E49.4.3")])],"isStart":false});
            var Q27;
            Q27=makeQuery(id+"F15.opExtrude","CAP_FACE",FACE,{"disambiguationData":[OSD([sQuery(id+"F14.wireOp",EDGE,"E49.3.0"),sQuery(id+"F14.wireOp",EDGE,"E49.3.1"),sQuery(id+"F14.wireOp",EDGE,"E49.3.2"),sQuery(id+"F14.wireOp",EDGE,"E49.3.3")])],"isStart":false});
            var Q28;
            Q28=makeQuery(id+"F15.opExtrude","CAP_FACE",FACE,{"disambiguationData":[OSD([sQuery(id+"F14.wireOp",EDGE,"E49.2.0"),sQuery(id+"F14.wireOp",EDGE,"E49.2.1"),sQuery(id+"F14.wireOp",EDGE,"E49.2.2"),sQuery(id+"F14.wireOp",EDGE,"E49.2.3")])],"isStart":false});
            var Q29;
            Q29=makeQuery(id+"F15.opExtrude","CAP_FACE",FACE,{"disambiguationData":[OSD([sQuery(id+"F14.wireOp",EDGE,"E49.1.0"),sQuery(id+"F14.wireOp",EDGE,"E49.1.1"),sQuery(id+"F14.wireOp",EDGE,"E49.1.2"),sQuery(id+"F14.wireOp",EDGE,"E49.1.3")])],"isStart":false});
            var Q30;
            Q30=makeQuery(id+"FpWToqtuObBjiHR_1.1.F15.opExtrude","CAP_FACE",FACE,{"disambiguationData":[OSD([sQuery(id+"F14.wireOp",EDGE,"E45"),sQuery(id+"F14.wireOp",EDGE,"E46.MirrorCS"),sQuery(id+"F14.wireOp",EDGE,"E47"),sQuery(id+"F14.wireOp",EDGE,"E48")])],"isStart":false});
            var Q31;
            Q31=makeQuery(id+"FpWToqtuObBjiHR_1.1.F15.opExtrude","CAP_FACE",FACE,{"disambiguationData":[OSD([sQuery(id+"F14.wireOp",EDGE,"E49.1.0"),sQuery(id+"F14.wireOp",EDGE,"E49.1.1"),sQuery(id+"F14.wireOp",EDGE,"E49.1.2"),sQuery(id+"F14.wireOp",EDGE,"E49.1.3")])],"isStart":false});
            var Q32;
            Q32=makeQuery(id+"FpWToqtuObBjiHR_1.1.F15.opExtrude","CAP_FACE",FACE,{"disambiguationData":[OSD([sQuery(id+"F14.wireOp",EDGE,"E49.2.0"),sQuery(id+"F14.wireOp",EDGE,"E49.2.1"),sQuery(id+"F14.wireOp",EDGE,"E49.2.2"),sQuery(id+"F14.wireOp",EDGE,"E49.2.3")])],"isStart":false});
            var Q33;
            Q33=makeQuery(id+"FpWToqtuObBjiHR_1.1.F15.opExtrude","CAP_FACE",FACE,{"disambiguationData":[OSD([sQuery(id+"F14.wireOp",EDGE,"E49.3.0"),sQuery(id+"F14.wireOp",EDGE,"E49.3.1"),sQuery(id+"F14.wireOp",EDGE,"E49.3.2"),sQuery(id+"F14.wireOp",EDGE,"E49.3.3")])],"isStart":false});
            var Q34;
            Q34=makeQuery(id+"FpWToqtuObBjiHR_1.1.F15.opExtrude","CAP_FACE",FACE,{"disambiguationData":[OSD([sQuery(id+"F14.wireOp",EDGE,"E49.4.0"),sQuery(id+"F14.wireOp",EDGE,"E49.4.1"),sQuery(id+"F14.wireOp",EDGE,"E49.4.2"),sQuery(id+"F14.wireOp",EDGE,"E49.4.3")])],"isStart":false});
            var Q35;
            Q35=makeQuery(id+"FpWToqtuObBjiHR_1.1.F15.opExtrude","CAP_FACE",FACE,{"disambiguationData":[OSD([sQuery(id+"F14.wireOp",EDGE,"E49.5.0"),sQuery(id+"F14.wireOp",EDGE,"E49.5.1"),sQuery(id+"F14.wireOp",EDGE,"E49.5.2"),sQuery(id+"F14.wireOp",EDGE,"E49.5.3")])],"isStart":false});
            var Q36;
            Q36=makeQuery(id+"FpWToqtuObBjiHR_1.1.F15.opExtrude","CAP_FACE",FACE,{"disambiguationData":[OSD([sQuery(id+"F14.wireOp",EDGE,"E49.6.0"),sQuery(id+"F14.wireOp",EDGE,"E49.6.1"),sQuery(id+"F14.wireOp",EDGE,"E49.6.2"),sQuery(id+"F14.wireOp",EDGE,"E49.6.3")])],"isStart":false});
            var Q37;
            Q37=makeQuery(id+"FpWToqtuObBjiHR_1.1.F15.opExtrude","CAP_FACE",FACE,{"disambiguationData":[OSD([sQuery(id+"F14.wireOp",EDGE,"E49.7.0"),sQuery(id+"F14.wireOp",EDGE,"E49.7.1"),sQuery(id+"F14.wireOp",EDGE,"E49.7.2"),sQuery(id+"F14.wireOp",EDGE,"E49.7.3")])],"isStart":false});
            var Q38;
            Q38=makeQuery(id+"FpWToqtuObBjiHR_1.1.F15.opExtrude","CAP_FACE",FACE,{"disambiguationData":[OSD([sQuery(id+"F14.wireOp",EDGE,"E49.8.0"),sQuery(id+"F14.wireOp",EDGE,"E49.8.1"),sQuery(id+"F14.wireOp",EDGE,"E49.8.2"),sQuery(id+"F14.wireOp",EDGE,"E49.8.3")])],"isStart":false});
            var Q39;
            Q39=makeQuery(id+"FpWToqtuObBjiHR_1.1.F15.opExtrude","CAP_FACE",FACE,{"disambiguationData":[OSD([sQuery(id+"F14.wireOp",EDGE,"E49.9.0"),sQuery(id+"F14.wireOp",EDGE,"E49.9.1"),sQuery(id+"F14.wireOp",EDGE,"E49.9.2"),sQuery(id+"F14.wireOp",EDGE,"E49.9.3")])],"isStart":false});
            var Q40;
            Q40=makeQuery(id+"FpWToqtuObBjiHR_1.1.F15.opExtrude","CAP_FACE",FACE,{"disambiguationData":[OSD([sQuery(id+"F14.wireOp",EDGE,"E49.10.0"),sQuery(id+"F14.wireOp",EDGE,"E49.10.1"),sQuery(id+"F14.wireOp",EDGE,"E49.10.2"),sQuery(id+"F14.wireOp",EDGE,"E49.10.3")])],"isStart":false});
            var Q41;
            Q41=makeQuery(id+"FpWToqtuObBjiHR_1.1.F15.opExtrude","CAP_FACE",FACE,{"disambiguationData":[OSD([sQuery(id+"F14.wireOp",EDGE,"E49.11.0"),sQuery(id+"F14.wireOp",EDGE,"E49.11.1"),sQuery(id+"F14.wireOp",EDGE,"E49.11.2"),sQuery(id+"F14.wireOp",EDGE,"E49.11.3")])],"isStart":false});
            var Q42;
            Q42=makeQuery(id+"FpWToqtuObBjiHR_1.1.F15.opExtrude","CAP_FACE",FACE,{"disambiguationData":[OSD([sQuery(id+"F14.wireOp",EDGE,"E49.12.0"),sQuery(id+"F14.wireOp",EDGE,"E49.12.1"),sQuery(id+"F14.wireOp",EDGE,"E49.12.2"),sQuery(id+"F14.wireOp",EDGE,"E49.12.3")])],"isStart":false});
            var Q43;
            Q43=makeQuery(id+"FpWToqtuObBjiHR_1.1.F15.opExtrude","CAP_FACE",FACE,{"disambiguationData":[OSD([sQuery(id+"F14.wireOp",EDGE,"E49.13.0"),sQuery(id+"F14.wireOp",EDGE,"E49.13.1"),sQuery(id+"F14.wireOp",EDGE,"E49.13.2"),sQuery(id+"F14.wireOp",EDGE,"E49.13.3")])],"isStart":false});
            var Q44;
            Q44=makeQuery(id+"FpWToqtuObBjiHR_1.1.F15.opExtrude","CAP_FACE",FACE,{"disambiguationData":[OSD([sQuery(id+"F14.wireOp",EDGE,"E49.14.0"),sQuery(id+"F14.wireOp",EDGE,"E49.14.1"),sQuery(id+"F14.wireOp",EDGE,"E49.14.2"),sQuery(id+"F14.wireOp",EDGE,"E49.14.3")])],"isStart":false});
            var Q45;
            Q45=makeQuery(id+"FpWToqtuObBjiHR_1.1.F15.opExtrude","CAP_FACE",FACE,{"disambiguationData":[OSD([sQuery(id+"F14.wireOp",EDGE,"E49.15.0"),sQuery(id+"F14.wireOp",EDGE,"E49.15.1"),sQuery(id+"F14.wireOp",EDGE,"E49.15.2"),sQuery(id+"F14.wireOp",EDGE,"E49.15.3")])],"isStart":false});
            var Q46;
            Q46=makeQuery(id+"FpWToqtuObBjiHR_1.1.F15.opExtrude","CAP_FACE",FACE,{"disambiguationData":[OSD([sQuery(id+"F14.wireOp",EDGE,"E49.16.0"),sQuery(id+"F14.wireOp",EDGE,"E49.16.1"),sQuery(id+"F14.wireOp",EDGE,"E49.16.2"),sQuery(id+"F14.wireOp",EDGE,"E49.16.3")])],"isStart":false});
            var Q47;
            Q47=makeQuery(id+"FpWToqtuObBjiHR_1.1.F15.opExtrude","CAP_FACE",FACE,{"disambiguationData":[OSD([sQuery(id+"F14.wireOp",EDGE,"E49.17.0"),sQuery(id+"F14.wireOp",EDGE,"E49.17.1"),sQuery(id+"F14.wireOp",EDGE,"E49.17.2"),sQuery(id+"F14.wireOp",EDGE,"E49.17.3")])],"isStart":false});
            var Q48;
            Q48=makeQuery(id+"FpWToqtuObBjiHR_1.1.F15.opExtrude","CAP_FACE",FACE,{"disambiguationData":[OSD([sQuery(id+"F14.wireOp",EDGE,"E49.18.0"),sQuery(id+"F14.wireOp",EDGE,"E49.18.1"),sQuery(id+"F14.wireOp",EDGE,"E49.18.2"),sQuery(id+"F14.wireOp",EDGE,"E49.18.3")])],"isStart":false});
            var Q49;
            Q49=makeQuery(id+"FpWToqtuObBjiHR_1.1.F15.opExtrude","CAP_FACE",FACE,{"disambiguationData":[OSD([sQuery(id+"F14.wireOp",EDGE,"E49.19.0"),sQuery(id+"F14.wireOp",EDGE,"E49.19.1"),sQuery(id+"F14.wireOp",EDGE,"E49.19.2"),sQuery(id+"F14.wireOp",EDGE,"E49.19.3")])],"isStart":false});
            var Q50;
            Q50=makeQuery(id+"FpWToqtuObBjiHR_1.1.F15.opExtrude","CAP_FACE",FACE,{"disambiguationData":[OSD([sQuery(id+"F14.wireOp",EDGE,"E49.20.0"),sQuery(id+"F14.wireOp",EDGE,"E49.20.1"),sQuery(id+"F14.wireOp",EDGE,"E49.20.2"),sQuery(id+"F14.wireOp",EDGE,"E49.20.3")])],"isStart":false});
            var Q51;
            Q51=makeQuery(id+"FpWToqtuObBjiHR_1.1.F15.opExtrude","CAP_FACE",FACE,{"disambiguationData":[OSD([sQuery(id+"F14.wireOp",EDGE,"E49.21.0"),sQuery(id+"F14.wireOp",EDGE,"E49.21.1"),sQuery(id+"F14.wireOp",EDGE,"E49.21.2"),sQuery(id+"F14.wireOp",EDGE,"E49.21.3")])],"isStart":false});
            var Q52;
            Q52=makeQuery(id+"FpWToqtuObBjiHR_1.1.F15.opExtrude","CAP_FACE",FACE,{"disambiguationData":[OSD([sQuery(id+"F14.wireOp",EDGE,"E49.22.0"),sQuery(id+"F14.wireOp",EDGE,"E49.22.1"),sQuery(id+"F14.wireOp",EDGE,"E49.22.2"),sQuery(id+"F14.wireOp",EDGE,"E49.22.3")])],"isStart":false});
            var Q53;
            Q53=makeQuery(id+"FpWToqtuObBjiHR_1.1.F15.opExtrude","CAP_FACE",FACE,{"disambiguationData":[OSD([sQuery(id+"F14.wireOp",EDGE,"E49.23.0"),sQuery(id+"F14.wireOp",EDGE,"E49.23.1"),sQuery(id+"F14.wireOp",EDGE,"E49.23.2"),sQuery(id+"F14.wireOp",EDGE,"E49.23.3")])],"isStart":false});
            var Q54;
            Q54=makeQuery(id+"FpWToqtuObBjiHR_1.1.F15.opExtrude","CAP_FACE",FACE,{"disambiguationData":[OSD([sQuery(id+"F14.wireOp",EDGE,"E49.24.0"),sQuery(id+"F14.wireOp",EDGE,"E49.24.1"),sQuery(id+"F14.wireOp",EDGE,"E49.24.2"),sQuery(id+"F14.wireOp",EDGE,"E49.24.3")])],"isStart":false});
            var Q55;
            Q55=makeQuery(id+"FpWToqtuObBjiHR_1.1.F15.opExtrude","CAP_FACE",FACE,{"disambiguationData":[OSD([sQuery(id+"F14.wireOp",EDGE,"E49.25.0"),sQuery(id+"F14.wireOp",EDGE,"E49.25.1"),sQuery(id+"F14.wireOp",EDGE,"E49.25.2"),sQuery(id+"F14.wireOp",EDGE,"E49.25.3")])],"isStart":false});
            var Q56;
            Q56=makeQuery(id+"FpWToqtuObBjiHR_1.1.F15.opExtrude","CAP_FACE",FACE,{"disambiguationData":[OSD([sQuery(id+"F14.wireOp",EDGE,"E49.26.0"),sQuery(id+"F14.wireOp",EDGE,"E49.26.1"),sQuery(id+"F14.wireOp",EDGE,"E49.26.2"),sQuery(id+"F14.wireOp",EDGE,"E49.26.3")])],"isStart":false});
            var Q57;
            Q57=makeQuery(id+"FpWToqtuObBjiHR_1.1.F15.opExtrude","CAP_FACE",FACE,{"disambiguationData":[OSD([sQuery(id+"F14.wireOp",EDGE,"E49.27.0"),sQuery(id+"F14.wireOp",EDGE,"E49.27.1"),sQuery(id+"F14.wireOp",EDGE,"E49.27.2"),sQuery(id+"F14.wireOp",EDGE,"E49.27.3")])],"isStart":false});
            var Q58;
            Q58=makeQuery(id+"FpWToqtuObBjiHR_1.1.F15.opExtrude","CAP_FACE",FACE,{"disambiguationData":[OSD([sQuery(id+"F14.wireOp",EDGE,"E49.28.0"),sQuery(id+"F14.wireOp",EDGE,"E49.28.1"),sQuery(id+"F14.wireOp",EDGE,"E49.28.2"),sQuery(id+"F14.wireOp",EDGE,"E49.28.3")])],"isStart":false});
            var Q59;
            Q59=makeQuery(id+"FpWToqtuObBjiHR_1.1.F15.opExtrude","CAP_FACE",FACE,{"disambiguationData":[OSD([sQuery(id+"F14.wireOp",EDGE,"E49.29.0"),sQuery(id+"F14.wireOp",EDGE,"E49.29.1"),sQuery(id+"F14.wireOp",EDGE,"E49.29.2"),sQuery(id+"F14.wireOp",EDGE,"E49.29.3")])],"isStart":false});
            fillet(context, id + "F16", {"entities" : qUnion([Q0, Q1, Q2, Q3, Q4, Q5, Q6, Q7, Q8, Q9, Q10, Q11, Q12, Q13, Q14, Q15, Q16, Q17, Q18, Q19, Q20, Q21, Q22, Q23, Q24, Q25, Q26, Q27, Q28, Q29, Q30, Q31, Q32, Q33, Q34, Q35, Q36, Q37, Q38, Q39, Q40, Q41, Q42, Q43, Q44, Q45, Q46, Q47, Q48, Q49, Q50, Q51, Q52, Q53, Q54, Q55, Q56, Q57, Q58, Q59]), "radius" : 1.27 * mm, "tangentPropagation" : true, "allowEdgeOverflow" : false});
        }
    });
